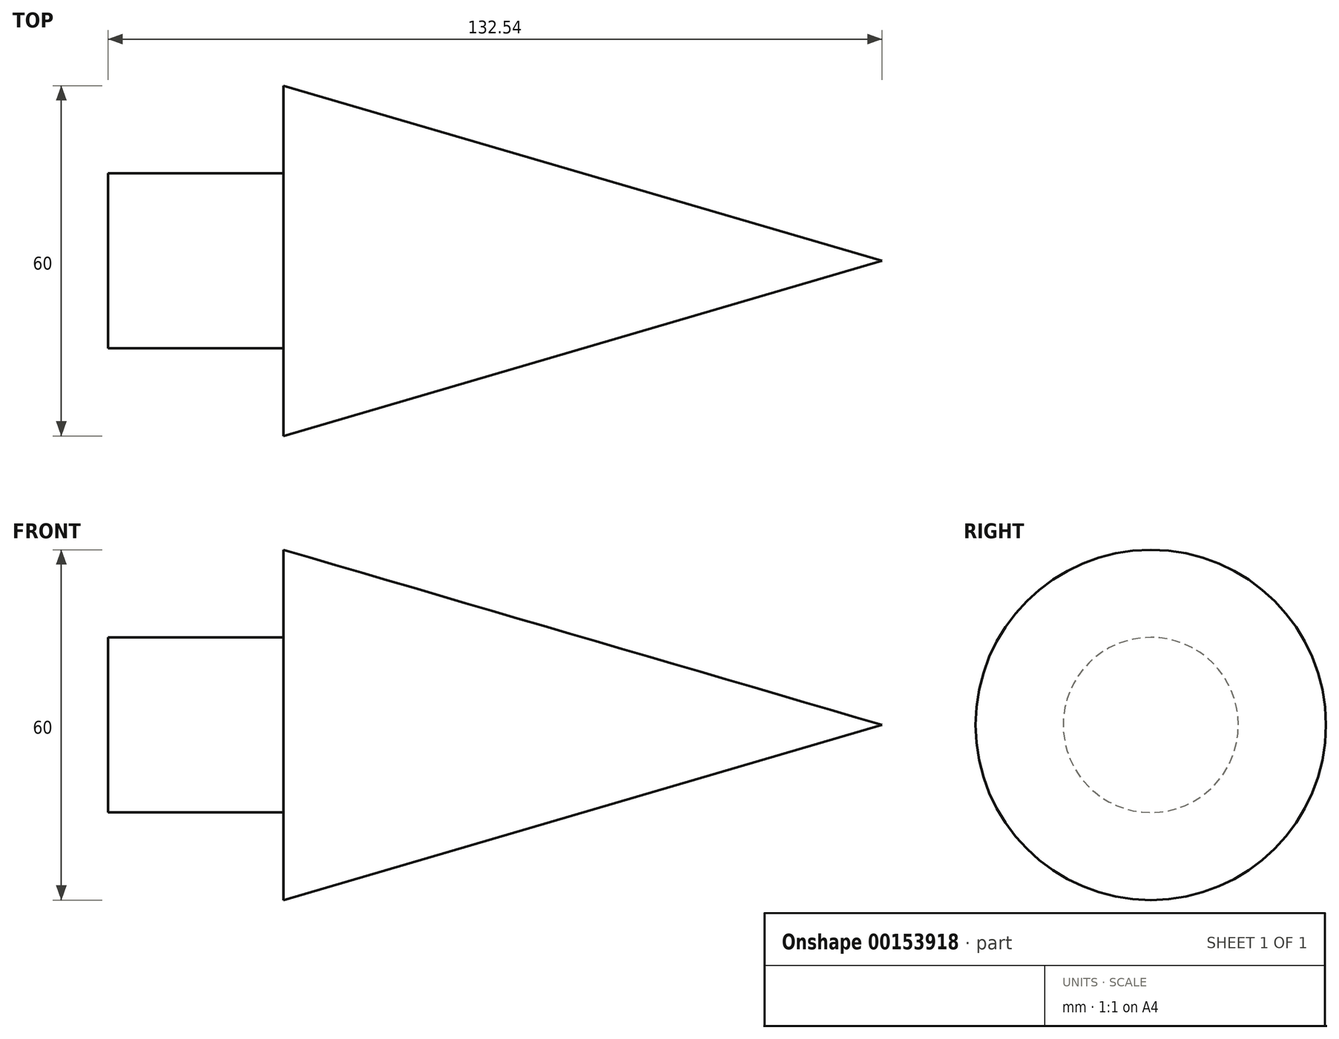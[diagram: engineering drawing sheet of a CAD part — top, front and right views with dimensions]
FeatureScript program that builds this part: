
annotation { "Feature Type Name" : "Feature", "Feature Type Description" : "" }
export const myFeature = defineFeature(function(context is Context, id is Id, definition is map)
    precondition{}
    {
        {
            var Q0;
            Q0=qCreatedBy(makeId("Top.planeOp"),FACE);
            var sketch = newSketch(context, id + "F0", { "sketchPlane" : qUnion([Q0])});
            skPoint(sketch, "E0", {"position": v(0, 15) * mm});
            skPoint(sketch, "E1", {"position": v(0, 30) * mm});
            skPoint(sketch, "E2", {"position": v(-30, 0) * mm});
            skLineSegment(sketch, "E3", {"start": v(-30, 0) * mm, "end": v(-30, 15) * mm});
            skLineSegment(sketch, "E4", {"start": v(-30, 15) * mm, "end": v(0, 15) * mm});
            skLineSegment(sketch, "E5", {"start": v(-30, 0) * mm, "end": v(102.54, 0) * mm});
            skLineSegment(sketch, "E6", {"start": v(0, 30) * mm, "end": v(102.54, 0) * mm});
            skLineSegment(sketch, "E7", {"start": v(0, 15) * mm, "end": v(0, 30) * mm});
            skSolve(sketch);
        }
        {
            var Q0;
            Q0=makeQuery(id+"F0.imprint","IMPRINT",FACE,{"disambiguationData":[TD([[makeQuery(id+"F0.imprint","IMPRINT",EDGE,{"derivedFrom":sQuery(id+"F0.wireOp",EDGE,"E3")}),-1.0]])]});
            var Q1;
            Q1=sQuery(id+"F0.wireOp",EDGE,"E5");
            revolve(context, id + "F1", {"entities" : qUnion([Q0]), "axis" : qUnion([Q1]), "revolveType" : RevolveType.FULL});
        }
    });
